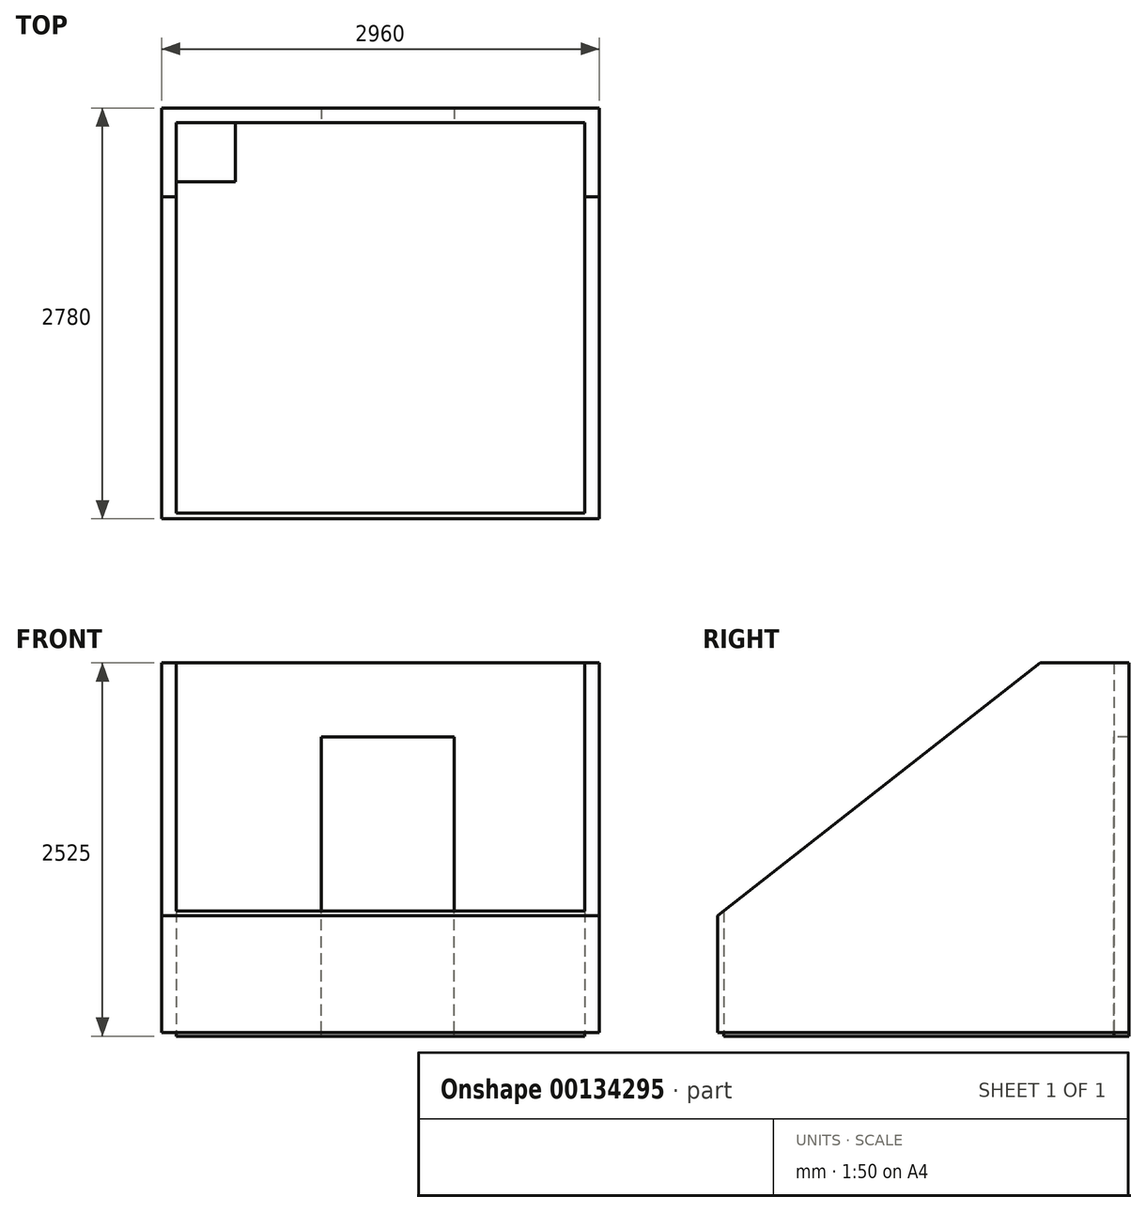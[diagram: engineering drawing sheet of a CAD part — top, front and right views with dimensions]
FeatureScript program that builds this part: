
annotation { "Feature Type Name" : "Feature", "Feature Type Description" : "" }
export const myFeature = defineFeature(function(context is Context, id is Id, definition is map)
    precondition{}
    {
        {
            var Q0;
            Q0=qCreatedBy(makeId("Top.planeOp"),FACE);
            var sketch = newSketch(context, id + "F0", { "sketchPlane" : qUnion([Q0])});
            skLineSegment(sketch, "E0.bottom", {"start": v(0, 0) * mm, "end": v(2960, 0) * mm});
            skLineSegment(sketch, "E0.top", {"start": v(0, 2780) * mm, "end": v(2960, 2780) * mm});
            skLineSegment(sketch, "E0.left", {"start": v(0, 0) * mm, "end": v(0, 2780) * mm});
            skLineSegment(sketch, "E0.right", {"start": v(2960, 0) * mm, "end": v(2960, 2780) * mm});
            skLineSegment(sketch, "E1.0", {"start": v(100, 40) * mm, "end": v(2860, 40) * mm});
            skLineSegment(sketch, "E1.1", {"start": v(100, 40) * mm, "end": v(100, 2680) * mm});
            skLineSegment(sketch, "E1.2", {"start": v(100, 2680) * mm, "end": v(2860, 2680) * mm});
            skLineSegment(sketch, "E1.3", {"start": v(2860, 40) * mm, "end": v(2860, 2680) * mm});
            skSolve(sketch);
        }
        {
            var Q0;
            Q0=makeQuery(id+"F0.imprint","IMPRINT",FACE,{"disambiguationData":[TD([[makeQuery(id+"F0.imprint","IMPRINT",EDGE,{"derivedFrom":sQuery(id+"F0.wireOp",EDGE,"E0.bottom")}),1.0]])]});
            extrude(context, id + "F1", {"entities" : qUnion([Q0]), "depth" : 2500 * mm});
        }
        {
            var Q0;
            Q0=makeQuery(id+"F1.opExtrude","SWEPT_FACE",FACE,{"disambiguationData":[OSD([sQuery(id+"F0.wireOp",EDGE,"E1.2")])]});
            var sketch = newSketch(context, id + "F2", { "sketchPlane" : qUnion([Q0])});
            skLineSegment(sketch, "E2", {"start": v(1980, 0) * mm, "end": v(1980, 2500) * mm});
            skLineSegment(sketch, "E3.bottom", {"start": v(1980, 0) * mm, "end": v(1080, 0) * mm});
            skLineSegment(sketch, "E3.top", {"start": v(1980, 2000) * mm, "end": v(1080, 2000) * mm});
            skLineSegment(sketch, "E3.left", {"start": v(1980, 0) * mm, "end": v(1980, 2000) * mm});
            skLineSegment(sketch, "E3.right", {"start": v(1080, 0) * mm, "end": v(1080, 2000) * mm});
            skSolve(sketch);
        }
        {
            var Q0;
            Q0 = qSketchRegion(id + "F2", true);
            extrude(context, id + "F3", {"entities" : qUnion([Q0]), "operationType" : NewBodyOperationType.REMOVE, "endBound" : BoundingType.UP_TO_NEXT, "oppositeDirection" : true, "depth" : 25 * mm});
        }
        {
            var Q0;
            Q0=makeQuery(id+"F1.opExtrude","CAP_FACE",FACE,{"disambiguationData":[OSD([sQuery(id+"F0.wireOp",EDGE,"E0.bottom"),sQuery(id+"F0.wireOp",EDGE,"E0.top"),sQuery(id+"F0.wireOp",EDGE,"E0.left"),sQuery(id+"F0.wireOp",EDGE,"E0.right"),sQuery(id+"F0.wireOp",EDGE,"E1.0"),sQuery(id+"F0.wireOp",EDGE,"E1.1"),sQuery(id+"F0.wireOp",EDGE,"E1.2"),sQuery(id+"F0.wireOp",EDGE,"E1.3")])],"isStart":true});
            var sketch = newSketch(context, id + "F4", { "sketchPlane" : qUnion([Q0])});
            skLineSegment(sketch, "E4.bottom", {"start": v(0, -2780) * mm, "end": v(2960, -2780) * mm});
            skLineSegment(sketch, "E4.top", {"start": v(0, 0) * mm, "end": v(2960, 0) * mm});
            skLineSegment(sketch, "E4.left", {"start": v(0, -2780) * mm, "end": v(0, 0) * mm});
            skLineSegment(sketch, "E4.right", {"start": v(2960, -2780) * mm, "end": v(2960, 0) * mm});
            skSolve(sketch);
        }
        {
            var Q0;
            {var subQ6=sQuery(id+"F0.wireOp",EDGE,"E1.0");Q0=makeQuery(id+"F4.imprint","IMPRINT",FACE,{"disambiguationData":[TD([[makeQuery(id+"F4.imprint","IMPRINT",EDGE,{"derivedFrom":makeQuery(id+"F1.opExtrude","CAP_EDGE",EDGE,{"disambiguationData":[OSD([subQ6])],"isStart":true})}),-1.0]])]});}
            extrude(context, id + "F5", {"entities" : qUnion([Q0]), "depth" : 25 * mm});
        }
        {
            var Q0;
            Q0=makeQuery(id+"F1.opExtrude","SWEPT_FACE",FACE,{"disambiguationData":[OSD([sQuery(id+"F0.wireOp",EDGE,"E0.right")])]});
            var sketch = newSketch(context, id + "F6", { "sketchPlane" : qUnion([Q0])});
            skLineSegment(sketch, "E5", {"start": v(0, 820) * mm, "end": v(40, 820) * mm});
            skLineSegment(sketch, "E6.0", {"start": v(40, 820) * mm, "end": v(40, 0) * mm});
            skLineSegment(sketch, "E7", {"start": v(40, 820) * mm, "end": v(2180, 2500) * mm});
            skPoint(sketch, "E8.orphan", {"position": v(40, 2500) * mm});
            skLineSegment(sketch, "E9", {"start": v(0, 788.6) * mm, "end": v(40, 820) * mm});
            skSolve(sketch);
        }
        {
            var Q0;
            Q0 = qSketchRegion(id + "F6", true);
            var Q1;
            {var subQ0=sQuery(id+"F6.wireOp",EDGE,"E5");Q1=makeQuery(id+"F6.imprint","IMPRINT",FACE,{"disambiguationData":[TD([[makeQuery(id+"F6.imprint","IMPRINT",EDGE,{"derivedFrom":subQ0}),1.0]])]});}
            extrude(context, id + "F7", {"entities" : qUnion([Q0, Q1]), "operationType" : NewBodyOperationType.REMOVE, "endBound" : BoundingType.THROUGH_ALL, "oppositeDirection" : true, "depth" : 25 * mm});
        }
        {
            var Q0;
            {var subQ0=sQuery(id+"F6.wireOp",EDGE,"E5");Q0=makeQuery(id+"F6.imprint","IMPRINT",FACE,{"disambiguationData":[TD([[makeQuery(id+"F6.imprint","IMPRINT",EDGE,{"derivedFrom":subQ0}),-1.0]])]});}
            extrude(context, id + "F8", {"entities" : qUnion([Q0]), "operationType" : NewBodyOperationType.REMOVE, "endBound" : BoundingType.UP_TO_NEXT, "oppositeDirection" : true, "depth" : 25 * mm});
        }
        {
            var Q0;
            Q0=makeQuery(id+"F0.imprint","IMPRINT",FACE,{"disambiguationData":[TD([[makeQuery(id+"F0.imprint","IMPRINT",EDGE,{"derivedFrom":sQuery(id+"F0.wireOp",EDGE,"E1.0")}),1.0]])]});
            var sketch = newSketch(context, id + "F9", { "sketchPlane" : qUnion([Q0])});
            skLineSegment(sketch, "E10.0", {"start": v(100, 40) * mm, "end": v(100, 2680) * mm, "construction": true});
            skLineSegment(sketch, "E11.0", {"start": v(100, 2680) * mm, "end": v(2860, 2680) * mm, "construction": true});
            skLineSegment(sketch, "E12.bottom", {"start": v(100, 2680) * mm, "end": v(500, 2680) * mm});
            skLineSegment(sketch, "E12.top", {"start": v(100, 2280) * mm, "end": v(500, 2280) * mm});
            skLineSegment(sketch, "E12.left", {"start": v(100, 2680) * mm, "end": v(100, 2280) * mm});
            skLineSegment(sketch, "E12.right", {"start": v(500, 2680) * mm, "end": v(500, 2280) * mm});
            skSolve(sketch);
        }
        {
            var Q0;
            Q0=makeQuery(id+"F9.imprint","IMPRINT",FACE,{"disambiguationData":[TD([[makeQuery(id+"F9.imprint","IMPRINT",EDGE,{"derivedFrom":sQuery(id+"F9.wireOp",EDGE,"E12.bottom")}),-1.0]])]});
            extrude(context, id + "F10", {"entities" : qUnion([Q0]), "depth" : 7 * mm});
        }
    });
